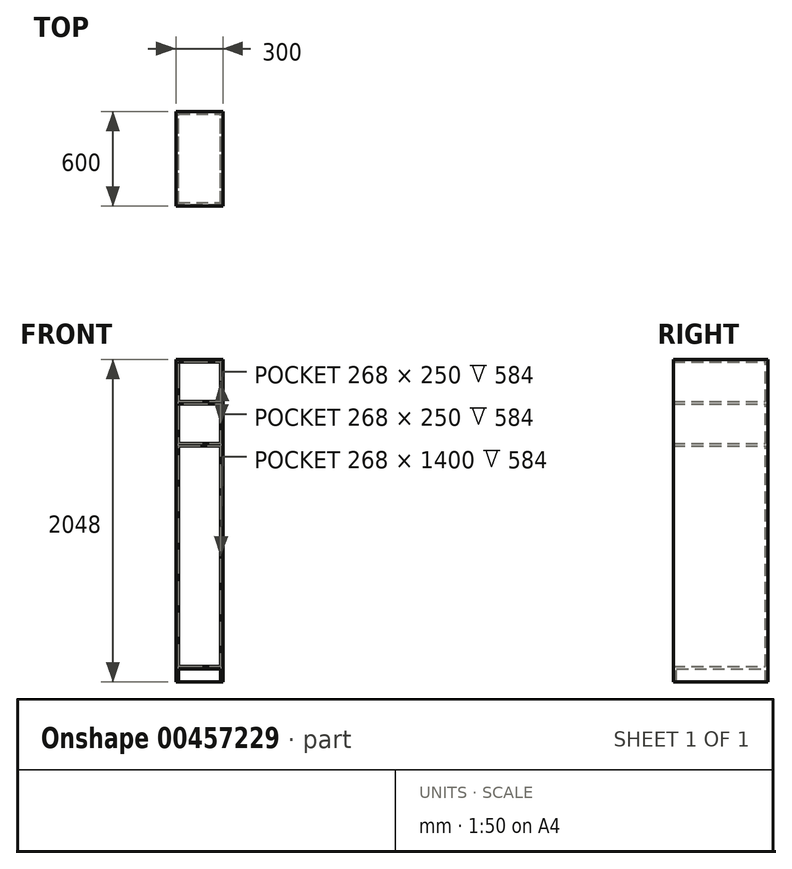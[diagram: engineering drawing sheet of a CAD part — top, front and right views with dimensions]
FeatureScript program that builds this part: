
annotation { "Feature Type Name" : "Feature", "Feature Type Description" : "" }
export const myFeature = defineFeature(function(context is Context, id is Id, definition is map)
    precondition{}
    {
        {
            var Q0;
            Q0=qCreatedBy(makeId("Front.planeOp"),FACE);
            var sketch = newSketch(context, id + "F0", { "sketchPlane" : qUnion([Q0])});
            skLineSegment(sketch, "E0.bottom", {"start": v(0, 0) * mm, "end": v(-16, 0) * mm});
            skLineSegment(sketch, "E0.top", {"start": v(0, 2048) * mm, "end": v(-300, 2048) * mm});
            skLineSegment(sketch, "E0.left", {"start": v(0, 0) * mm, "end": v(0, 2048) * mm});
            skLineSegment(sketch, "E0.right", {"start": v(-300, 0) * mm, "end": v(-300, 2048) * mm});
            skLineSegment(sketch, "E1.bottom", {"start": v(-284, 100) * mm, "end": v(-16, 100) * mm});
            skLineSegment(sketch, "E1.top", {"start": v(-284, 2032) * mm, "end": v(-16, 2032) * mm});
            skLineSegment(sketch, "E1.left", {"start": v(-284, 100) * mm, "end": v(-284, 2032) * mm});
            skLineSegment(sketch, "E1.right", {"start": v(-16, 100) * mm, "end": v(-16, 2032) * mm});
            skLineSegment(sketch, "E2.top", {"start": v(-284, 84) * mm, "end": v(-16, 84) * mm});
            skLineSegment(sketch, "E2.left", {"start": v(-284, 0) * mm, "end": v(-284, 84) * mm});
            skLineSegment(sketch, "E2.right", {"start": v(-16, 0) * mm, "end": v(-16, 84) * mm});
            skLineSegment(sketch, "E3.trimOffspring", {"start": v(-284, 0) * mm, "end": v(-300, 0) * mm});
            skLineSegment(sketch, "E4", {"start": v(-284, 0) * mm, "end": v(-16, 0) * mm});
            skLineSegment(sketch, "E5", {"start": v(-284, 1516) * mm, "end": v(-16, 1516) * mm});
            skLineSegment(sketch, "E6", {"start": v(-284, 1500) * mm, "end": v(-16, 1500) * mm});
            skLineSegment(sketch, "E7", {"start": v(-284, 1766) * mm, "end": v(-16, 1766) * mm});
            skLineSegment(sketch, "E8", {"start": v(-284, 1782) * mm, "end": v(-16, 1782) * mm});
            skSolve(sketch);
        }
        {
            var Q0;
            Q0=makeQuery(id+"F0.imprint","IMPRINT",FACE,{"disambiguationData":[TD([[makeQuery(id+"F0.imprint","IMPRINT",EDGE,{"derivedFrom":sQuery(id+"F0.wireOp",EDGE,"E0.bottom")}),-1.0]])]});
            var Q1;
            Q1=makeQuery(id+"F0.imprint","IMPRINT",FACE,{"disambiguationData":[TD([[makeQuery(id+"F0.imprint","IMPRINT",EDGE,{"derivedFrom":sQuery(id+"F0.wireOp",EDGE,"E2.top")}),-1.0]])]});
            var Q2;
            Q2=makeQuery(id+"F0.imprint","IMPRINT",FACE,{"disambiguationData":[TD([[makeQuery(id+"F0.imprint","IMPRINT",EDGE,{"derivedFrom":sQuery(id+"F0.wireOp",EDGE,"E1.bottom")}),1.0]])]});
            var Q3;
            {var subQ0=sQuery(id+"F0.wireOp",EDGE,"E5");Q3=makeQuery(id+"F0.imprint","IMPRINT",FACE,{"disambiguationData":[TD([[makeQuery(id+"F0.imprint","IMPRINT",EDGE,{"derivedFrom":subQ0}),-1.0]])]});}
            var Q4;
            {var subQ0=sQuery(id+"F0.wireOp",EDGE,"E5");Q4=makeQuery(id+"F0.imprint","IMPRINT",FACE,{"disambiguationData":[TD([[makeQuery(id+"F0.imprint","IMPRINT",EDGE,{"derivedFrom":subQ0}),1.0]])]});}
            var Q5;
            {var subQ0=sQuery(id+"F0.wireOp",EDGE,"E7");Q5=makeQuery(id+"F0.imprint","IMPRINT",FACE,{"disambiguationData":[TD([[makeQuery(id+"F0.imprint","IMPRINT",EDGE,{"derivedFrom":subQ0}),1.0]])]});}
            var Q6;
            {var subQ0=sQuery(id+"F0.wireOp",EDGE,"E1.top");Q6=makeQuery(id+"F0.imprint","IMPRINT",FACE,{"disambiguationData":[TD([[makeQuery(id+"F0.imprint","IMPRINT",EDGE,{"derivedFrom":subQ0}),-1.0]])]});}
            extrude(context, id + "F1", {"entities" : qUnion([Q0, Q1, Q2, Q3, Q4, Q5, Q6]), "oppositeDirection" : true, "depth" : 16 * mm});
        }
        {
            var Q0;
            Q0=makeQuery(id+"F0.imprint","IMPRINT",FACE,{"disambiguationData":[TD([[makeQuery(id+"F0.imprint","IMPRINT",EDGE,{"derivedFrom":sQuery(id+"F0.wireOp",EDGE,"E0.bottom")}),-1.0]])]});
            var Q1;
            {var subQ0=sQuery(id+"F0.wireOp",EDGE,"E5");Q1=makeQuery(id+"F0.imprint","IMPRINT",FACE,{"disambiguationData":[TD([[makeQuery(id+"F0.imprint","IMPRINT",EDGE,{"derivedFrom":subQ0}),-1.0]])]});}
            var Q2;
            {var subQ0=sQuery(id+"F0.wireOp",EDGE,"E7");Q2=makeQuery(id+"F0.imprint","IMPRINT",FACE,{"disambiguationData":[TD([[makeQuery(id+"F0.imprint","IMPRINT",EDGE,{"derivedFrom":subQ0}),1.0]])]});}
            extrude(context, id + "F2", {"entities" : qUnion([Q0, Q1, Q2]), "operationType" : NewBodyOperationType.ADD, "depth" : 584 * mm});
        }
        {
            var Q0;
            Q0=makeQuery(id+"F2.opExtrude","SWEPT_FACE",FACE,{"disambiguationData":[OSD([sQuery(id+"F0.wireOp",EDGE,"E2.top")])]});
            var sketch = newSketch(context, id + "F3", { "sketchPlane" : qUnion([Q0])});
            skPoint(sketch, "E9.0", {"position": v(-284, 584) * mm});
            skPoint(sketch, "E10.0", {"position": v(-16, 584) * mm});
            skLineSegment(sketch, "E11.bottom", {"start": v(-284, 579) * mm, "end": v(-16, 579) * mm});
            skLineSegment(sketch, "E11.top", {"start": v(-284, 563) * mm, "end": v(-16, 563) * mm});
            skLineSegment(sketch, "E11.left", {"start": v(-284, 579) * mm, "end": v(-284, 563) * mm});
            skLineSegment(sketch, "E11.right", {"start": v(-16, 579) * mm, "end": v(-16, 563) * mm});
            skSolve(sketch);
        }
        {
            var Q0;
            Q0=makeQuery(id+"F3.imprint","IMPRINT",FACE,{"disambiguationData":[TD([[makeQuery(id+"F3.imprint","IMPRINT",EDGE,{"derivedFrom":sQuery(id+"F3.wireOp",EDGE,"E11.bottom")}),-1.0]])]});
            var Q1;
            {var subQ0=sQuery(id+"F0.wireOp",EDGE,"E3.trimOffspring");var subQ1=sQuery(id+"F0.wireOp",EDGE,"E0.bottom");Q1=makeQuery(id+"F2.boolean.opBoolean","MERGE",FACE,{"derivedFrom":[makeQuery(id+"F1.opExtrude","SWEPT_FACE",FACE,{"disambiguationData":[OSD([subQ1,subQ0,sQuery(id+"F0.wireOp",EDGE,"E4")])]}),makeQuery(id+"F2.opExtrude","SWEPT_FACE",FACE,{"disambiguationData":[OSD([subQ1])]}),makeQuery(id+"F2.opExtrude","SWEPT_FACE",FACE,{"disambiguationData":[OSD([subQ0])]})]});}
            extrude(context, id + "F4", {"entities" : qUnion([Q0]), "operationType" : NewBodyOperationType.ADD, "endBound" : BoundingType.UP_TO_SURFACE, "endBoundEntityFace" : qUnion([Q1]), "depth" : 25 * mm});
        }
    });
